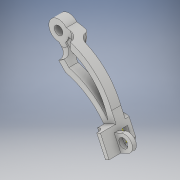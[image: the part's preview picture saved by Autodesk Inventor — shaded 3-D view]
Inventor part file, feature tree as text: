
AUTODESK INVENTOR PART (.ipt)
format: ipt  version: 2018 (Build 220112000, 112)  size: 317,952 bytes
history: native  units: in
note: dims shown in document units (in); Inventor stores cm internally (conversion verified against a paired STEP export)
features: sketch x14, extrude x10, fillet x2, plane x1
ambient origin geometry x8: Origin, YZ Plane, XZ Plane, XY Plane, X Axis, Y Axis, Z Axis, Center Point
bodies: Solid1 (feature_tree)
feature tree (27):
  sketch  "Sketch1"  dims[d15=1.0in d47=0.1969in d48=0.1969in]
  extrude  "Extrusion12"  Depth=0.1969in
  sketch  "Sketch16"  dims[d63=2.1654in d64=0.1969in]
  extrude  "Extrusion16"  Depth=0.1969in
  extrude  "Extrusion19"  Depth=0.7874in
  plane  "Work Plane9"
  sketch  "Sketch25"  dims[d75=0.2559in d76=0.2756in d77=0.0in]
  sketch  "Sketch26"  dims[d101=0.1181in d102=0.3937in d103=0.0in d106=0.5906in]
  extrude  "Extrusion20"  Depth=0.1969in
  sketch  "Sketch30"  dims[d118=0.4724in d119=0.1181in]
  extrude  "Extrusion21"  Depth=0.2756in TaperAngle=0.0deg
  extrude  "Extrusion22"  Depth=0.3937in TaperAngle=0.0deg
  fillet  "Fillet5"  Radius=0.5906in
  extrude  "Extrusion25"  Depth=0.1575in TaperAngle=0.0deg
  extrude  "Extrusion26"  Depth=0.1181in
  extrude  "Extrusion27"  Depth=0.2165in
  extrude  "Extrusion28"  Depth=0.4724in TaperAngle=0.0deg
  fillet  "Fillet6"  Radius=0.2362in
  sketch  "Sketch19"  dims[d65=0.1969in d66=0.7874in]
  sketch  "Sketch24"  dims[d68=0.1969in d74=0.1969in]
  sketch  "Sketch27"  dims[d115=0.5906in d116=0.1575in d117=0.0in]
  sketch  "Sketch31"  dims[d120=0.374in d121=0.2165in]
  sketch  "Sketch32"  dims[d122=0.2362in d123=0.4724in d124=0.0in d129=0.2362in]
  sketch  "Sketch35"  dims[d130=0.1181in]
  sketch  "Sketch36"  dims[d131=0.2362in]
  sketch  "Sketch37"  dims[d132=0.1181in]
  sketch  "Sketch38"  dims[d133=0.4724in d134=0.0in d135=0.1516in d136=0.0in d139=0.1969in d140=0.2756in d141=0.1181in d142=0.0in d143=0.2362in d153=0.2756in d154=0.0in d155=0.1181in d156=0.0in d157=1.1811in d158=0.2362in d159=0.0in d160=1.1811in d161=0.2756in d162=0.2756in d163=0.0in d164=0.1969in d165=0.0787in d166=0.1181in d167=0.1575in]
